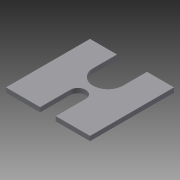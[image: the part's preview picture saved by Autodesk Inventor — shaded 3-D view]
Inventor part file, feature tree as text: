
AUTODESK INVENTOR PART (.ipt)
format: ipt  version: 2013 (Build 170138000, 138)  size: 90,112 bytes
history: native  units: in
note: dims shown in document units (in); Inventor stores cm internally (conversion verified against a paired STEP export)
features: extrude x1, mirror x1, sketch x1
ambient origin geometry x8: Origin, YZ Plane, XZ Plane, XY Plane, X Axis, Y Axis, Z Axis, Center Point
bodies: Solid1 (feature_tree)
feature tree (3):
  extrude  "Extrusion1"  Depth=0.5in
  mirror  "Mirror1"
  sketch  "Sketch1"  dims[d2=0.715in d8=0.5in d9=3.5in d11=1.75in d12=0.1875in d13=0.0in d14=1.0in d15=0.625in]
